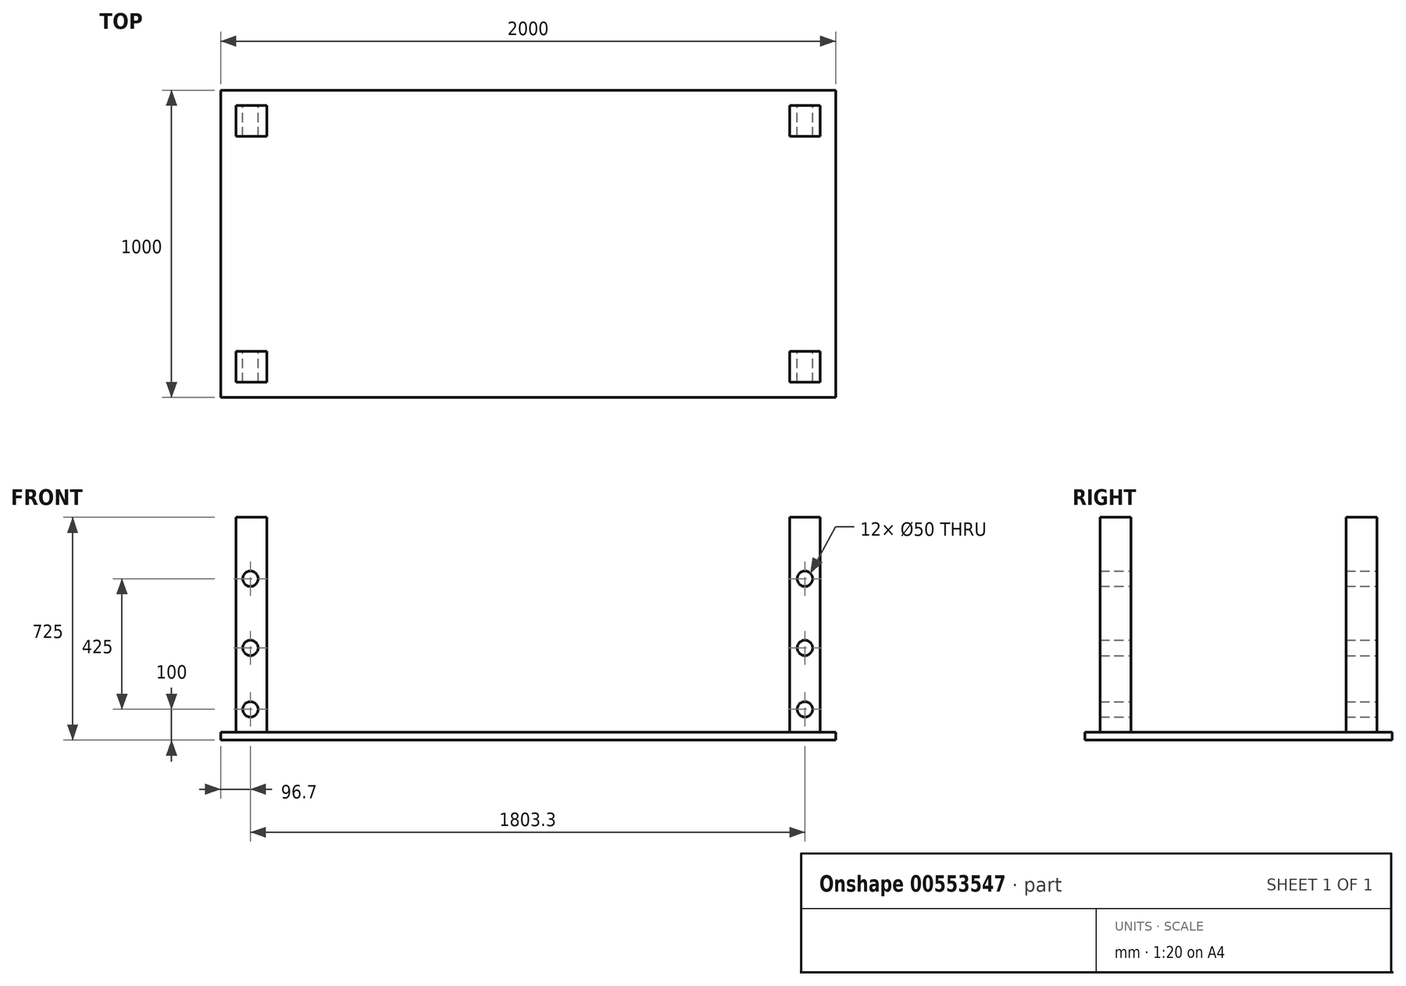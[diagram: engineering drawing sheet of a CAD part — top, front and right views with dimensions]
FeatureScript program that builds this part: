
annotation { "Feature Type Name" : "Feature", "Feature Type Description" : "" }
export const myFeature = defineFeature(function(context is Context, id is Id, definition is map)
    precondition{}
    {
        {
            var Q0;
            Q0=qCreatedBy(makeId("Top.planeOp"),FACE);
            var sketch = newSketch(context, id + "F0", { "sketchPlane" : qUnion([Q0])});
            skLineSegment(sketch, "E0.bottom", {"start": v(-96.7, 968.92) * mm, "end": v(1903.3, 968.92) * mm});
            skLineSegment(sketch, "E0.top", {"start": v(-96.7, -31.08) * mm, "end": v(1903.3, -31.08) * mm});
            skLineSegment(sketch, "E0.left", {"start": v(-96.7, 968.92) * mm, "end": v(-96.7, -31.08) * mm});
            skLineSegment(sketch, "E0.right", {"start": v(1903.3, 968.92) * mm, "end": v(1903.3, -31.08) * mm});
            skSolve(sketch);
        }
        {
            var Q0;
            Q0 = qSketchRegion(id + "F0", true);
            extrude(context, id + "F1", {"entities" : qUnion([Q0]), "depth" : 25 * mm, "offsetDistance" : 25 * mm});
        }
        {
            var Q0;
            Q0=qCreatedBy(makeId("Top.planeOp"),FACE);
            var sketch = newSketch(context, id + "F2", { "sketchPlane" : qUnion([Q0])});
            skLineSegment(sketch, "E1.bottom", {"start": v(-46.7, 118.92) * mm, "end": v(53.3, 118.92) * mm});
            skLineSegment(sketch, "E1.top", {"start": v(-46.7, 18.92) * mm, "end": v(53.3, 18.92) * mm});
            skLineSegment(sketch, "E1.left", {"start": v(-46.7, 118.92) * mm, "end": v(-46.7, 18.92) * mm});
            skLineSegment(sketch, "E1.right", {"start": v(53.3, 118.92) * mm, "end": v(53.3, 18.92) * mm});
            skLineSegment(sketch, "E2.bottom", {"start": v(1753.3, 118.92) * mm, "end": v(1853.3, 118.92) * mm});
            skLineSegment(sketch, "E2.top", {"start": v(1753.3, 18.92) * mm, "end": v(1853.3, 18.92) * mm});
            skLineSegment(sketch, "E2.left", {"start": v(1753.3, 118.92) * mm, "end": v(1753.3, 18.92) * mm});
            skLineSegment(sketch, "E2.right", {"start": v(1853.3, 118.92) * mm, "end": v(1853.3, 18.92) * mm});
            skLineSegment(sketch, "E3.bottom", {"start": v(1753.3, 918.92) * mm, "end": v(1853.3, 918.92) * mm});
            skLineSegment(sketch, "E3.top", {"start": v(1753.3, 818.92) * mm, "end": v(1853.3, 818.92) * mm});
            skLineSegment(sketch, "E3.left", {"start": v(1753.3, 918.92) * mm, "end": v(1753.3, 818.92) * mm});
            skLineSegment(sketch, "E3.right", {"start": v(1853.3, 918.92) * mm, "end": v(1853.3, 818.92) * mm});
            skLineSegment(sketch, "E4.bottom", {"start": v(-46.7, 918.92) * mm, "end": v(53.3, 918.92) * mm});
            skLineSegment(sketch, "E4.top", {"start": v(-46.7, 818.92) * mm, "end": v(53.3, 818.92) * mm});
            skLineSegment(sketch, "E4.left", {"start": v(-46.7, 918.92) * mm, "end": v(-46.7, 818.92) * mm});
            skLineSegment(sketch, "E4.right", {"start": v(53.3, 918.92) * mm, "end": v(53.3, 818.92) * mm});
            skSolve(sketch);
        }
        {
            var Q0;
            Q0 = qSketchRegion(id + "F2", true);
            extrude(context, id + "F3", {"entities" : qUnion([Q0]), "operationType" : NewBodyOperationType.ADD, "depth" : 725 * mm, "offsetDistance" : 25 * mm});
        }
        {
            var Q0;
            Q0=makeQuery(id+"F3.opExtrude","SWEPT_FACE",FACE,{"disambiguationData":[OSD([sQuery(id+"F2.wireOp",EDGE,"E4.bottom")])]});
            var sketch = newSketch(context, id + "F4", { "sketchPlane" : qUnion([Q0])});
            skCircle(sketch, "E5", {"center": v(0, 300) * mm, "radius": 25 * mm});
            skCircle(sketch, "E6", {"center": v(0, 525) * mm, "radius": 25 * mm});
            skCircle(sketch, "E7", {"center": v(0, 100) * mm, "radius": 25 * mm});
            skCircle(sketch, "E8", {"center": v(-1803.3, 100) * mm, "radius": 25 * mm});
            skCircle(sketch, "E9", {"center": v(-1803.3, 300) * mm, "radius": 25 * mm});
            skCircle(sketch, "E10", {"center": v(-1803.3, 525) * mm, "radius": 25 * mm});
            skSolve(sketch);
        }
        {
            var Q0;
            Q0 = qSketchRegion(id + "F4", true);
            extrude(context, id + "F5", {"entities" : qUnion([Q0]), "operationType" : NewBodyOperationType.REMOVE, "endBound" : BoundingType.THROUGH_ALL, "oppositeDirection" : true, "depth" : 50 * mm, "offsetDistance" : 25 * mm});
        }
    });
